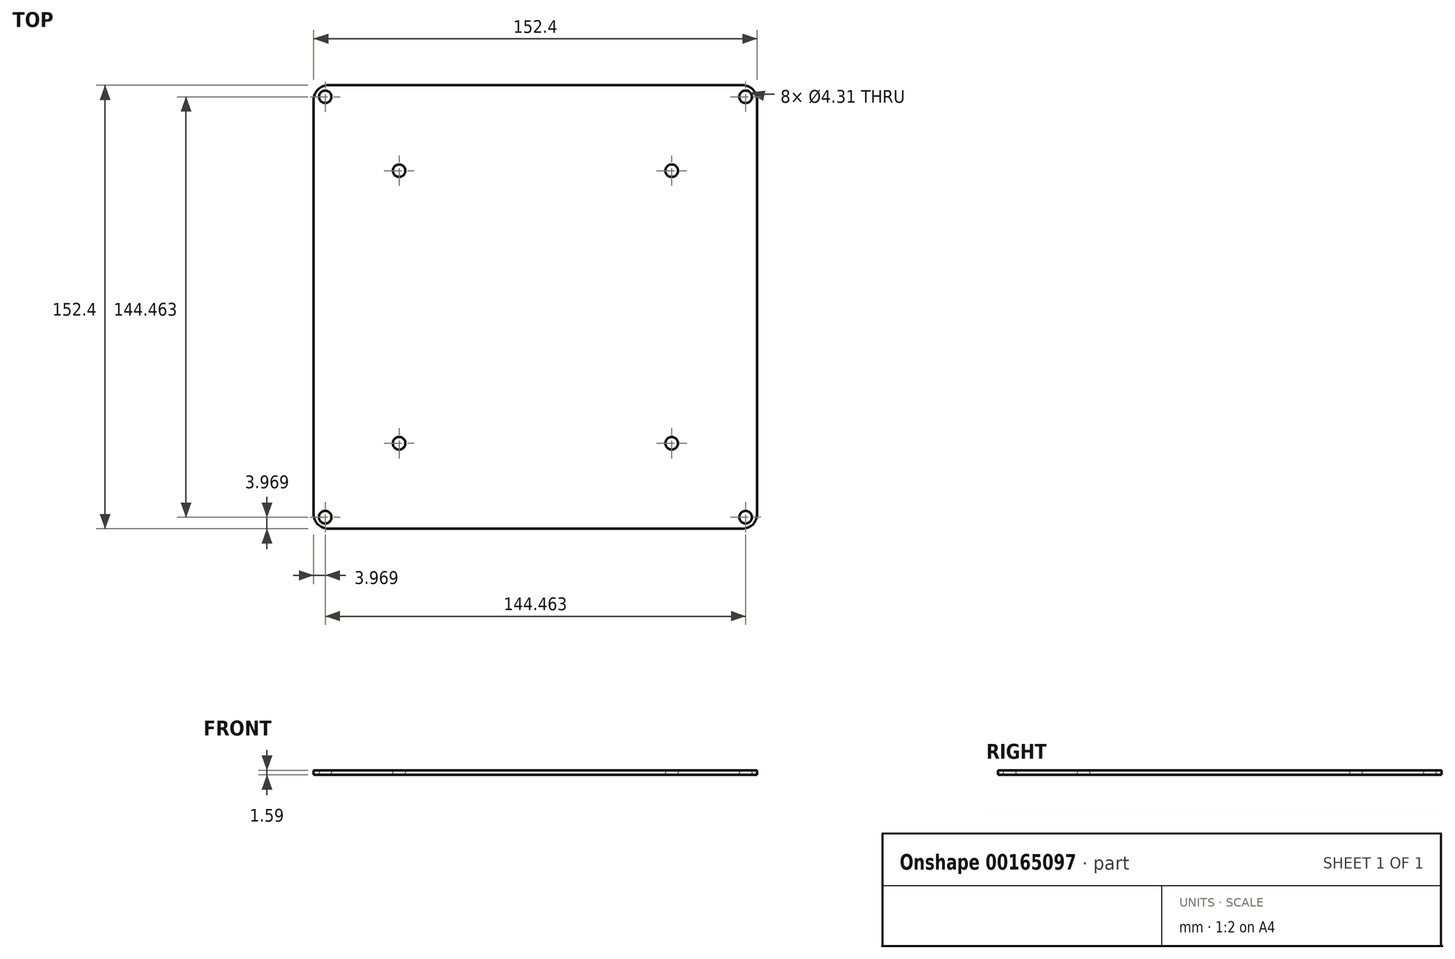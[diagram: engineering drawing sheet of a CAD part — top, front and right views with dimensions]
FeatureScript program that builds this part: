
annotation { "Feature Type Name" : "Feature", "Feature Type Description" : "" }
export const myFeature = defineFeature(function(context is Context, id is Id, definition is map)
    precondition{}
    {
        {
            var Q0;
            Q0=qCreatedBy(makeId("Top.planeOp"),FACE);
            var sketch = newSketch(context, id + "F0", { "sketchPlane" : qUnion([Q0])});
            skLineSegment(sketch, "E0.bottom", {"start": v(-72.23, 72.23) * mm, "end": v(72.23, 72.23) * mm, "construction": true});
            skLineSegment(sketch, "E0.top", {"start": v(-72.23, -72.23) * mm, "end": v(72.23, -72.23) * mm, "construction": true});
            skLineSegment(sketch, "E0.left", {"start": v(-72.23, 72.23) * mm, "end": v(-72.23, -72.23) * mm, "construction": true});
            skLineSegment(sketch, "E0.right", {"start": v(72.23, 72.23) * mm, "end": v(72.23, -72.23) * mm, "construction": true});
            skPoint(sketch, "E0.middle", {"position": v(0, 0) * mm});
            skCircle(sketch, "E1", {"center": v(-72.23, -72.23) * mm, "radius": 2.15 * mm});
            skCircle(sketch, "E2", {"center": v(-72.23, 72.23) * mm, "radius": 2.15 * mm});
            skCircle(sketch, "E3", {"center": v(72.23, 72.23) * mm, "radius": 2.15 * mm});
            skCircle(sketch, "E4", {"center": v(72.23, -72.23) * mm, "radius": 2.15 * mm});
            skLineSegment(sketch, "E5.bottom", {"start": v(46.83, -46.83) * mm, "end": v(-46.83, -46.83) * mm, "construction": true});
            skLineSegment(sketch, "E5.top", {"start": v(46.83, 46.83) * mm, "end": v(-46.83, 46.83) * mm, "construction": true});
            skLineSegment(sketch, "E5.left", {"start": v(46.83, -46.83) * mm, "end": v(46.83, 46.83) * mm, "construction": true});
            skLineSegment(sketch, "E5.right", {"start": v(-46.83, -46.83) * mm, "end": v(-46.83, 46.83) * mm, "construction": true});
            skCircle(sketch, "E6", {"center": v(-46.83, 46.83) * mm, "radius": 2.15 * mm});
            skCircle(sketch, "E7", {"center": v(46.83, 46.83) * mm, "radius": 2.15 * mm});
            skCircle(sketch, "E8", {"center": v(46.83, -46.83) * mm, "radius": 2.15 * mm});
            skCircle(sketch, "E9", {"center": v(-46.83, -46.83) * mm, "radius": 2.15 * mm});
            skLineSegment(sketch, "E10.bottom", {"start": v(76.2, -76.2) * mm, "end": v(-76.2, -76.2) * mm});
            skLineSegment(sketch, "E10.top", {"start": v(76.2, 76.2) * mm, "end": v(-76.2, 76.2) * mm});
            skLineSegment(sketch, "E10.left", {"start": v(76.2, -76.2) * mm, "end": v(76.2, 76.2) * mm});
            skLineSegment(sketch, "E10.right", {"start": v(-76.2, -76.2) * mm, "end": v(-76.2, 76.2) * mm});
            skLineSegment(sketch, "E11", {"start": v(0, 72.23) * mm, "end": v(0, 76.2) * mm, "construction": true});
            skSolve(sketch);
        }
        {
            var Q0;
            Q0 = qSketchRegion(id + "F0", true);
            extrude(context, id + "F1", {"entities" : qUnion([Q0]), "depth" : 1.59 * mm});
        }
        {
            var Q0;
            Q0=makeQuery(id+"F1.opExtrude","SWEPT_EDGE",EDGE,{"disambiguationData":[OSD([sQuery(id+"F0.wireOp",EDGE,"E10.top"),sQuery(id+"F0.wireOp",EDGE,"E10.right")])]});
            var Q1;
            Q1=makeQuery(id+"F1.opExtrude","SWEPT_EDGE",EDGE,{"disambiguationData":[OSD([sQuery(id+"F0.wireOp",EDGE,"E10.top"),sQuery(id+"F0.wireOp",EDGE,"E10.left")])]});
            var Q2;
            Q2=makeQuery(id+"F1.opExtrude","SWEPT_EDGE",EDGE,{"disambiguationData":[OSD([sQuery(id+"F0.wireOp",EDGE,"E10.bottom"),sQuery(id+"F0.wireOp",EDGE,"E10.left")])]});
            var Q3;
            Q3=makeQuery(id+"F1.opExtrude","SWEPT_EDGE",EDGE,{"disambiguationData":[OSD([sQuery(id+"F0.wireOp",EDGE,"E10.bottom"),sQuery(id+"F0.wireOp",EDGE,"E10.right")])]});
            fillet(context, id + "F2", {"entities" : qUnion([Q0, Q1, Q2, Q3]), "radius" : 5.08 * mm, "tangentPropagation" : true, "allowEdgeOverflow" : false});
        }
    });
